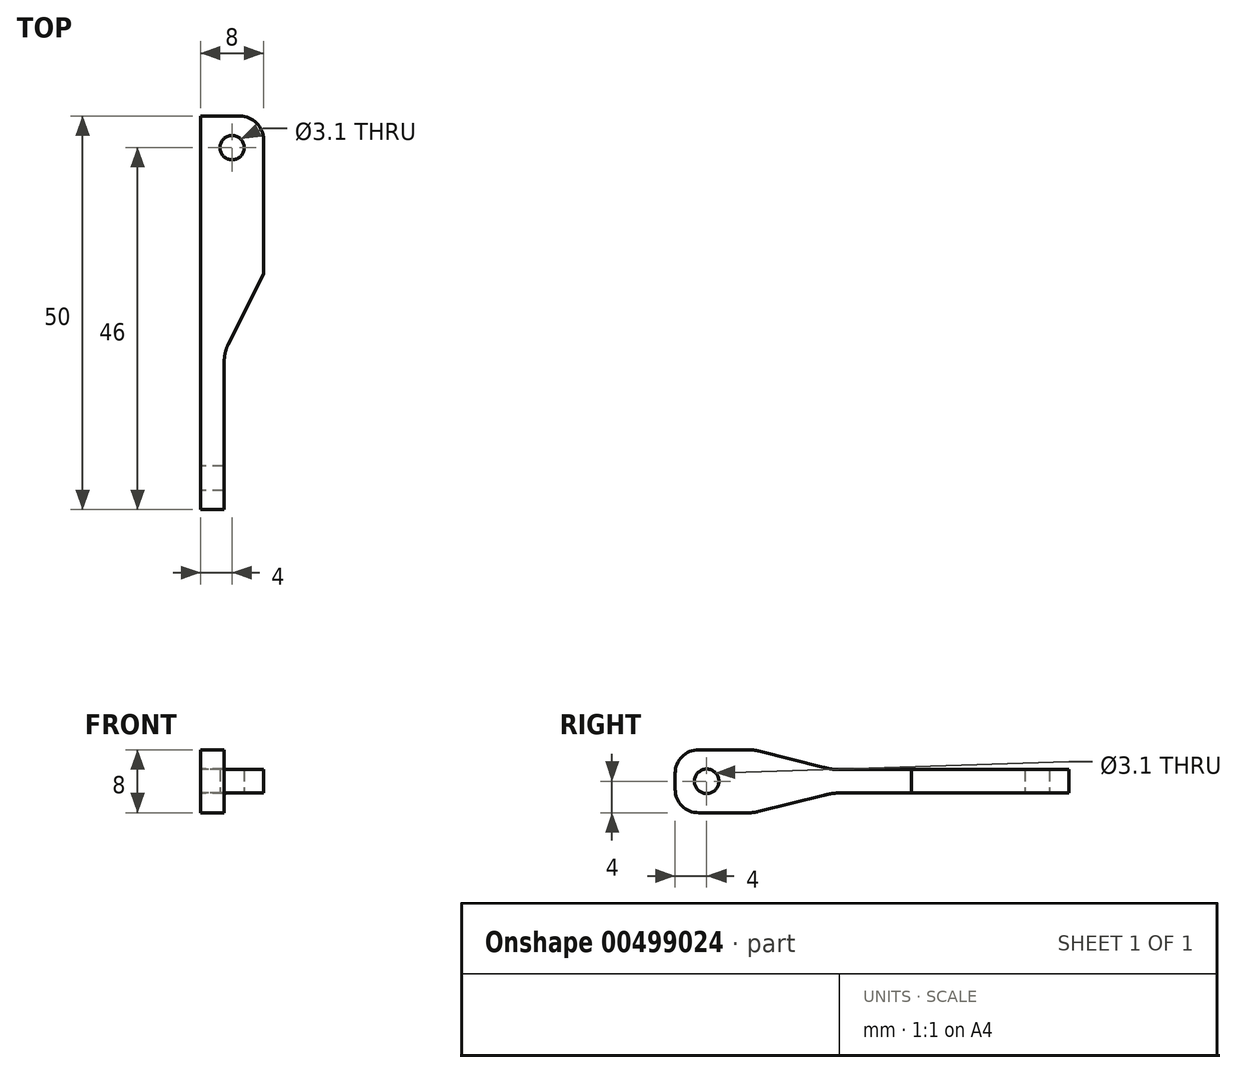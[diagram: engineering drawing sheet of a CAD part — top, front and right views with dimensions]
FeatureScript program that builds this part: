
annotation { "Feature Type Name" : "Feature", "Feature Type Description" : "" }
export const myFeature = defineFeature(function(context is Context, id is Id, definition is map)
    precondition{}
    {
        {
            var Q0;
            Q0=qCreatedBy(makeId("Right.planeOp"),FACE);
            var sketch = newSketch(context, id + "F0", { "sketchPlane" : qUnion([Q0])});
            skLineSegment(sketch, "E0.bottom", {"start": v(-25, 4) * mm, "end": v(25, 4) * mm});
            skLineSegment(sketch, "E0.top", {"start": v(-25, -4) * mm, "end": v(25, -4) * mm});
            skLineSegment(sketch, "E0.left", {"start": v(-25, 4) * mm, "end": v(-25, -4) * mm});
            skLineSegment(sketch, "E0.right", {"start": v(25, 4) * mm, "end": v(25, -4) * mm});
            skPoint(sketch, "E1", {"position": v(0, 4) * mm});
            skPoint(sketch, "E2", {"position": v(-25, 0) * mm});
            skCircle(sketch, "E3", {"center": v(-21, 0) * mm, "radius": 1.55 * mm});
            skLineSegment(sketch, "E4.bottom", {"start": v(-5, 1.5) * mm, "end": v(25, 1.5) * mm});
            skLineSegment(sketch, "E4.top", {"start": v(-5, -1.5) * mm, "end": v(25, -1.5) * mm});
            skLineSegment(sketch, "E4.left", {"start": v(-5, 1.5) * mm, "end": v(-5, -1.5) * mm});
            skLineSegment(sketch, "E4.right", {"start": v(25, 1.5) * mm, "end": v(25, -1.5) * mm});
            skPoint(sketch, "E5", {"position": v(-5, 0) * mm});
            skLineSegment(sketch, "E6", {"start": v(-15, 4) * mm, "end": v(-5, 1.5) * mm});
            skLineSegment(sketch, "E7", {"start": v(-5, -1.5) * mm, "end": v(-15, -4) * mm});
            skSolve(sketch);
        }
        {
            var Q0;
            {var subQ0=sQuery(id+"F0.wireOp",EDGE,"E0.left");Q0=makeQuery(id+"F0.imprint","IMPRINT",FACE,{"disambiguationData":[TD([[makeQuery(id+"F0.imprint","IMPRINT",EDGE,{"derivedFrom":subQ0}),1.0]])]});}
            var Q1;
            Q1=makeQuery(id+"F0.imprint","IMPRINT",FACE,{"disambiguationData":[TD([[makeQuery(id+"F0.imprint","IMPRINT",EDGE,{"derivedFrom":sQuery(id+"F0.wireOp",EDGE,"E4.bottom")}),-1.0]])]});
            extrude(context, id + "F1", {"entities" : qUnion([Q0, Q1]), "depth" : 3 * mm, "offsetDistance" : 25 * mm});
        }
        {
            var Q0;
            Q0=makeQuery(id+"F1.opExtrude","CAP_FACE",FACE,{"disambiguationData":[OSD([sQuery(id+"F0.wireOp",EDGE,"E0.bottom"),sQuery(id+"F0.wireOp",EDGE,"E0.top"),sQuery(id+"F0.wireOp",EDGE,"E0.left"),sQuery(id+"F0.wireOp",EDGE,"E3"),sQuery(id+"F0.wireOp",EDGE,"E4.bottom"),sQuery(id+"F0.wireOp",EDGE,"E4.top"),sQuery(id+"F0.wireOp",EDGE,"E4.right"),sQuery(id+"F0.wireOp",EDGE,"E6"),sQuery(id+"F0.wireOp",EDGE,"E7")])],"isStart":false});
            var sketch = newSketch(context, id + "F2", { "sketchPlane" : qUnion([Q0])});
            skLineSegment(sketch, "E8.bottom", {"start": v(25, 1.5) * mm, "end": v(-5, 1.5) * mm});
            skLineSegment(sketch, "E8.top", {"start": v(25, -1.5) * mm, "end": v(-5, -1.5) * mm});
            skLineSegment(sketch, "E8.left", {"start": v(25, 1.5) * mm, "end": v(25, -1.5) * mm});
            skLineSegment(sketch, "E8.right", {"start": v(-5, 1.5) * mm, "end": v(-5, -1.5) * mm});
            skSolve(sketch);
        }
        {
            var Q0;
            Q0=makeQuery(id+"F2.imprint","IMPRINT",FACE,{"disambiguationData":[TD([[makeQuery(id+"F2.imprint","IMPRINT",EDGE,{"derivedFrom":sQuery(id+"F2.wireOp",EDGE,"E8.bottom")}),-1.0]])]});
            extrude(context, id + "F3", {"entities" : qUnion([Q0]), "operationType" : NewBodyOperationType.ADD, "depth" : 5 * mm, "offsetDistance" : 25 * mm});
        }
        {
            var Q0;
            Q0=makeQuery(id+"F3.boolean.opBoolean","MERGE",FACE,{"derivedFrom":[makeQuery(id+"F1.opExtrude","SWEPT_FACE",FACE,{"disambiguationData":[OSD([sQuery(id+"F0.wireOp",EDGE,"E4.top")])]}),makeQuery(id+"F3.opExtrude","SWEPT_FACE",FACE,{"disambiguationData":[OSD([sQuery(id+"F2.wireOp",EDGE,"E8.top")])]})]});
            var sketch = newSketch(context, id + "F4", { "sketchPlane" : qUnion([Q0])});
            skLineSegment(sketch, "E9", {"start": v(3, 5) * mm, "end": v(8, -5) * mm});
            skLineSegment(sketch, "E10", {"start": v(8, -5) * mm, "end": v(8, 5) * mm});
            skLineSegment(sketch, "E11", {"start": v(8, 5) * mm, "end": v(3, 5) * mm});
            skPoint(sketch, "E12", {"position": v(4, -25) * mm});
            skCircle(sketch, "E13", {"center": v(4, -21) * mm, "radius": 1.55 * mm});
            skSolve(sketch);
        }
        {
            var Q0;
            Q0=makeQuery(id+"F4.imprint","IMPRINT",FACE,{"disambiguationData":[TD([[makeQuery(id+"F4.imprint","IMPRINT",EDGE,{"derivedFrom":sQuery(id+"F4.wireOp",EDGE,"E9")}),1.0]])]});
            var Q1;
            Q1=makeQuery(id+"F4.imprint","IMPRINT",FACE,{"disambiguationData":[TD([[makeQuery(id+"F4.imprint","IMPRINT",EDGE,{"derivedFrom":sQuery(id+"F4.wireOp",EDGE,"E13")}),1.0]])]});
            extrude(context, id + "F5", {"entities" : qUnion([Q0, Q1]), "operationType" : NewBodyOperationType.REMOVE, "endBound" : BoundingType.UP_TO_NEXT, "oppositeDirection" : true, "depth" : 25 * mm, "offsetDistance" : 25 * mm});
        }
        {
            var Q0;
            Q0=makeQuery(id+"F1.opExtrude","SWEPT_EDGE",EDGE,{"disambiguationData":[OSD([sQuery(id+"F0.wireOp",EDGE,"E0.bottom"),sQuery(id+"F0.wireOp",EDGE,"E0.left")])]});
            var Q1;
            Q1=makeQuery(id+"F1.opExtrude","SWEPT_EDGE",EDGE,{"disambiguationData":[OSD([sQuery(id+"F0.wireOp",EDGE,"E0.top"),sQuery(id+"F0.wireOp",EDGE,"E0.left")])]});
            var Q2;
            Q2=makeQuery(id+"F3.opExtrude","CAP_EDGE",EDGE,{"disambiguationData":[OSD([sQuery(id+"F2.wireOp",EDGE,"E8.left")])],"isStart":false});
            fillet(context, id + "F6", {"entities" : qUnion([Q0, Q1, Q2]), "radius" : 3 * mm, "tangentPropagation" : true, "allowEdgeOverflow" : false});
        }
        {
            var Q0;
            {var subQ0=sQuery(id+"F2.wireOp",EDGE,"E8.right");Q0=makeQuery(id+"F5.boolean.opBoolean","MERGE",EDGE,{"derivedFrom":[makeQuery(id+"F3.opExtrude","CAP_EDGE",EDGE,{"disambiguationData":[OSD([subQ0])],"isStart":true})],"fromTools":[makeQuery(id+"F5.opExtrude","SWEPT_EDGE",EDGE,{"disambiguationData":[OSD([sQuery(id+"F0.wireOp",EDGE,"E4.bottom"),sQuery(id+"F0.wireOp",EDGE,"E4.left"),sQuery(id+"F0.wireOp",EDGE,"E6"),sQuery(id+"F2.wireOp",EDGE,"E8.bottom"),subQ0])]})]});}
            var Q1;
            Q1=makeQuery(id+"F5.boolean.opBoolean","COPY",EDGE,{"derivedFrom":makeQuery(id+"F5.opExtrude","SWEPT_EDGE",EDGE,{"disambiguationData":[OSD([sQuery(id+"F2.wireOp",EDGE,"E8.top"),sQuery(id+"F4.wireOp",EDGE,"E9"),sQuery(id+"F4.wireOp",EDGE,"E10")])]})});
            var Q2;
            Q2=makeQuery(id+"F1.opExtrude","SWEPT_EDGE",EDGE,{"disambiguationData":[OSD([sQuery(id+"F0.wireOp",EDGE,"E4.bottom"),sQuery(id+"F0.wireOp",EDGE,"E4.left"),sQuery(id+"F0.wireOp",EDGE,"E6")])]});
            var Q3;
            Q3=makeQuery(id+"F1.opExtrude","SWEPT_EDGE",EDGE,{"disambiguationData":[OSD([sQuery(id+"F0.wireOp",EDGE,"E4.top"),sQuery(id+"F0.wireOp",EDGE,"E4.left"),sQuery(id+"F0.wireOp",EDGE,"E7")])]});
            var Q4;
            Q4=makeQuery(id+"F1.opExtrude","SWEPT_EDGE",EDGE,{"disambiguationData":[OSD([sQuery(id+"F0.wireOp",EDGE,"E0.bottom"),sQuery(id+"F0.wireOp",EDGE,"E6")])]});
            var Q5;
            Q5=makeQuery(id+"F1.opExtrude","SWEPT_EDGE",EDGE,{"disambiguationData":[OSD([sQuery(id+"F0.wireOp",EDGE,"E0.top"),sQuery(id+"F0.wireOp",EDGE,"E7")])]});
            fillet(context, id + "F7", {"entities" : qUnion([Q0, Q1, Q2, Q3, Q4, Q5]), "radius" : 5 * mm, "tangentPropagation" : true, "allowEdgeOverflow" : false});
        }
    });
